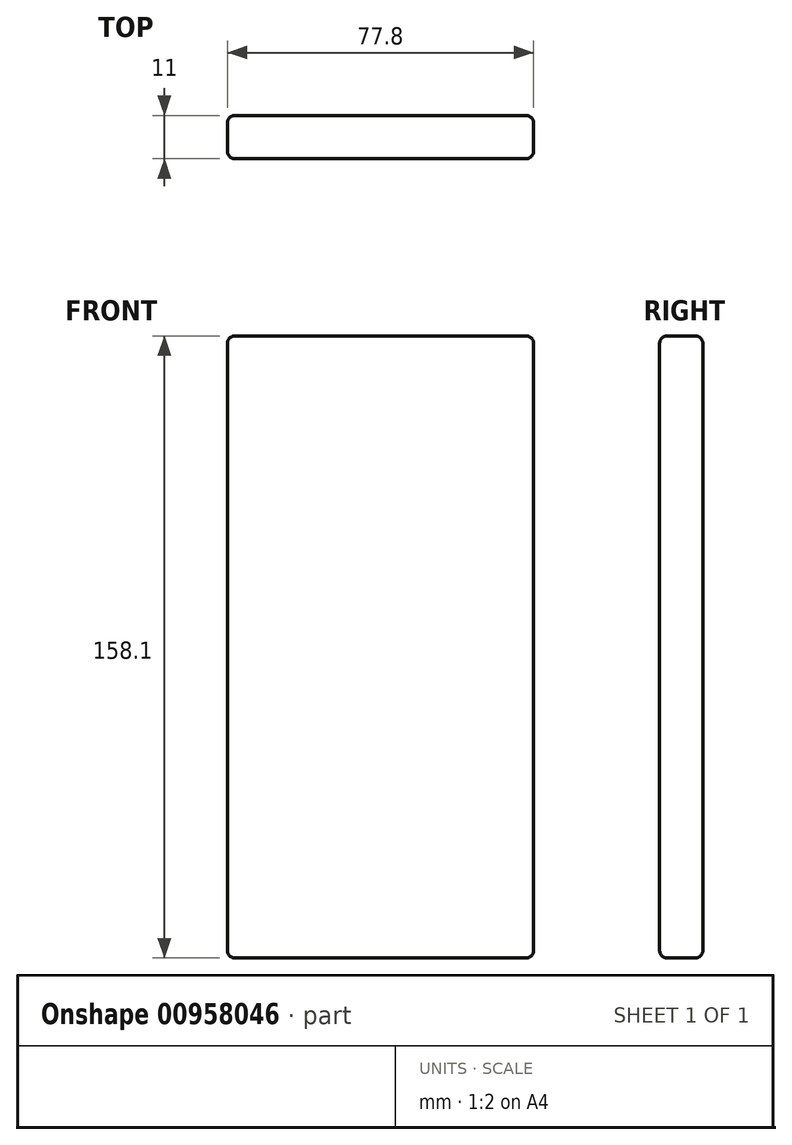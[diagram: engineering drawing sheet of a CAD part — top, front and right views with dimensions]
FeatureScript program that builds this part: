
annotation { "Feature Type Name" : "Feature", "Feature Type Description" : "" }
export const myFeature = defineFeature(function(context is Context, id is Id, definition is map)
    precondition{}
    {
        {
            var Q0;
            Q0=qCreatedBy(makeId("Top.planeOp"),FACE);
            var sketch = newSketch(context, id + "F0", { "sketchPlane" : qUnion([Q0])});
            skLineSegment(sketch, "E0.bottom", {"start": v(38.9, -5.5) * mm, "end": v(-38.9, -5.5) * mm});
            skLineSegment(sketch, "E0.top", {"start": v(38.9, 5.5) * mm, "end": v(-38.9, 5.5) * mm});
            skLineSegment(sketch, "E0.left", {"start": v(38.9, -5.5) * mm, "end": v(38.9, 5.5) * mm});
            skLineSegment(sketch, "E0.right", {"start": v(-38.9, -5.5) * mm, "end": v(-38.9, 5.5) * mm});
            skPoint(sketch, "E0.middle", {"position": v(0, 0) * mm});
            skSolve(sketch);
        }
        {
            var Q0;
            Q0 = qSketchRegion(id + "F0", true);
            extrude(context, id + "F1", {"entities" : qUnion([Q0]), "depth" : 158.1 * mm, "offsetDistance" : 25 * mm});
        }
        {
            var Q0;
            Q0=makeQuery(id+"F1.opExtrude","SWEPT_FACE",FACE,{"disambiguationData":[OSD([sQuery(id+"F0.wireOp",EDGE,"E0.bottom")])]});
            var Q1;
            Q1=makeQuery(id+"F1.opExtrude","SWEPT_FACE",FACE,{"disambiguationData":[OSD([sQuery(id+"F0.wireOp",EDGE,"E0.top")])]});
            var Q2;
            Q2=makeQuery(id+"F1.opExtrude","CAP_FACE",FACE,{"disambiguationData":[OSD([sQuery(id+"F0.wireOp",EDGE,"E0.bottom"),sQuery(id+"F0.wireOp",EDGE,"E0.top"),sQuery(id+"F0.wireOp",EDGE,"E0.left"),sQuery(id+"F0.wireOp",EDGE,"E0.right")])],"isStart":false});
            var Q3;
            Q3=makeQuery(id+"F1.opExtrude","CAP_FACE",FACE,{"disambiguationData":[OSD([sQuery(id+"F0.wireOp",EDGE,"E0.bottom"),sQuery(id+"F0.wireOp",EDGE,"E0.top"),sQuery(id+"F0.wireOp",EDGE,"E0.left"),sQuery(id+"F0.wireOp",EDGE,"E0.right")])],"isStart":true});
            fillet(context, id + "F2", {"entities" : qUnion([Q0, Q1, Q2, Q3]), "radius" : 2 * mm, "tangentPropagation" : true, "allowEdgeOverflow" : false});
        }
    });
